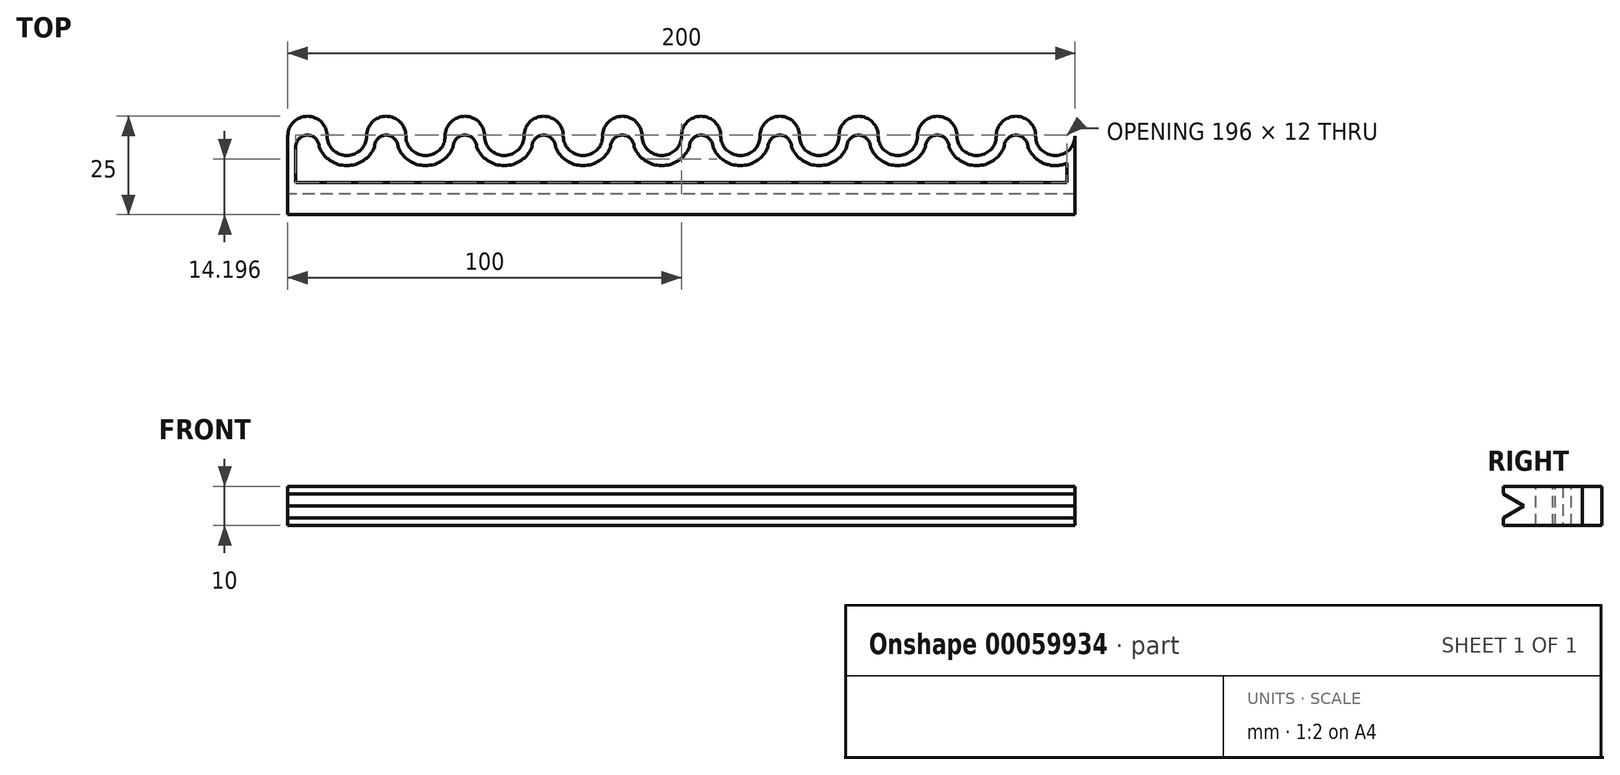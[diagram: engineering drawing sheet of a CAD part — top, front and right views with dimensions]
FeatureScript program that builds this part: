
annotation { "Feature Type Name" : "Feature", "Feature Type Description" : "" }
export const myFeature = defineFeature(function(context is Context, id is Id, definition is map)
    precondition{}
    {
        {
            var Q0;
            Q0=qCreatedBy(makeId("Top.planeOp"),FACE);
            var sketch = newSketch(context, id + "F0", { "sketchPlane" : qUnion([Q0])});
            skArc(sketch, "E0", {"start": v(10, 20) * mm, "mid": v(5, 25) * mm, "end": v(0, 20) * mm});
            skArc(sketch, "E1", {"start": v(10, 20) * mm, "mid": v(15, 15) * mm, "end": v(20, 20) * mm});
            skLineSegment(sketch, "E2", {"start": v(0, 20) * mm, "end": v(20, 20) * mm, "construction": true});
            skArc(sketch, "E3.1.0.0", {"start": v(30, 20) * mm, "mid": v(25, 25) * mm, "end": v(20, 20) * mm});
            skArc(sketch, "E3.1.0.1", {"start": v(30, 20) * mm, "mid": v(35, 15) * mm, "end": v(40, 20) * mm});
            skArc(sketch, "E3.2.0.0", {"start": v(50, 20) * mm, "mid": v(45, 25) * mm, "end": v(40, 20) * mm});
            skArc(sketch, "E3.2.0.1", {"start": v(50, 20) * mm, "mid": v(55, 15) * mm, "end": v(60, 20) * mm});
            skArc(sketch, "E3.3.0.0", {"start": v(70, 20) * mm, "mid": v(65, 25) * mm, "end": v(60, 20) * mm});
            skArc(sketch, "E3.3.0.1", {"start": v(70, 20) * mm, "mid": v(75, 15) * mm, "end": v(80, 20) * mm});
            skArc(sketch, "E3.4.0.0", {"start": v(90, 20) * mm, "mid": v(85, 25) * mm, "end": v(80, 20) * mm});
            skArc(sketch, "E3.4.0.1", {"start": v(90, 20) * mm, "mid": v(95, 15) * mm, "end": v(100, 20) * mm});
            skArc(sketch, "E3.5.0.0", {"start": v(110, 20) * mm, "mid": v(105, 25) * mm, "end": v(100, 20) * mm});
            skArc(sketch, "E3.5.0.1", {"start": v(110, 20) * mm, "mid": v(115, 15) * mm, "end": v(120, 20) * mm});
            skArc(sketch, "E3.6.0.0", {"start": v(130, 20) * mm, "mid": v(125, 25) * mm, "end": v(120, 20) * mm});
            skArc(sketch, "E3.6.0.1", {"start": v(130, 20) * mm, "mid": v(135, 15) * mm, "end": v(140, 20) * mm});
            skArc(sketch, "E3.7.0.0", {"start": v(150, 20) * mm, "mid": v(145, 25) * mm, "end": v(140, 20) * mm});
            skArc(sketch, "E3.7.0.1", {"start": v(150, 20) * mm, "mid": v(155, 15) * mm, "end": v(160, 20) * mm});
            skArc(sketch, "E3.8.0.0", {"start": v(170, 20) * mm, "mid": v(165, 25) * mm, "end": v(160, 20) * mm});
            skArc(sketch, "E3.8.0.1", {"start": v(170, 20) * mm, "mid": v(175, 15) * mm, "end": v(180, 20) * mm});
            skArc(sketch, "E3.9.0.0", {"start": v(190, 20) * mm, "mid": v(185, 25) * mm, "end": v(180, 20) * mm});
            skArc(sketch, "E3.9.0.1", {"start": v(190, 20) * mm, "mid": v(195, 15) * mm, "end": v(200, 20) * mm});
            skLineSegment(sketch, "E4", {"start": v(0, 20) * mm, "end": v(0, 0) * mm});
            skLineSegment(sketch, "E5", {"start": v(0, 0) * mm, "end": v(200, 0) * mm});
            skLineSegment(sketch, "E6", {"start": v(200, 0) * mm, "end": v(200, 20) * mm});
            skSolve(sketch);
        }
        {
            var Q0;
            Q0=makeQuery(id+"F0.imprint","IMPRINT",FACE,{"disambiguationData":[TD([[makeQuery(id+"F0.imprint","IMPRINT",EDGE,{"derivedFrom":sQuery(id+"F0.wireOp",EDGE,"E0")}),1.0]])]});
            extrude(context, id + "F1", {"entities" : qUnion([Q0]), "depth" : 10 * mm});
        }
        {
            var Q0;
            Q0=makeQuery(id+"F1.opExtrude","SWEPT_FACE",FACE,{"disambiguationData":[OSD([sQuery(id+"F0.wireOp",EDGE,"E4")])]});
            var sketch = newSketch(context, id + "F2", { "sketchPlane" : qUnion([Q0])});
            skLineSegment(sketch, "E7", {"start": v(0, 8) * mm, "end": v(-5.2, 5) * mm});
            skLineSegment(sketch, "E8", {"start": v(-5.2, 5) * mm, "end": v(0, 2) * mm});
            skLineSegment(sketch, "E9", {"start": v(0, 2) * mm, "end": v(0, 8) * mm});
            skLineSegment(sketch, "E10", {"start": v(0, 10) * mm, "end": v(0, 8) * mm});
            skLineSegment(sketch, "E11", {"start": v(0, 2) * mm, "end": v(0, 0) * mm});
            skSolve(sketch);
        }
        {
            var Q0;
            Q0=makeQuery(id+"F2.imprint","IMPRINT",FACE,{"disambiguationData":[TD([[makeQuery(id+"F2.imprint","IMPRINT",EDGE,{"derivedFrom":sQuery(id+"F2.wireOp",EDGE,"E7")}),1.0]])]});
            extrude(context, id + "F3", {"entities" : qUnion([Q0]), "operationType" : NewBodyOperationType.REMOVE, "endBound" : BoundingType.THROUGH_ALL, "oppositeDirection" : true, "depth" : 25 * mm});
        }
        {
            var Q0;
            Q0=makeQuery(id+"F1.opExtrude","CAP_FACE",FACE,{"disambiguationData":[OSD([sQuery(id+"F0.wireOp",EDGE,"E0"),sQuery(id+"F0.wireOp",EDGE,"E1"),sQuery(id+"F0.wireOp",EDGE,"E3.1.0.0"),sQuery(id+"F0.wireOp",EDGE,"E3.1.0.1"),sQuery(id+"F0.wireOp",EDGE,"E3.2.0.0"),sQuery(id+"F0.wireOp",EDGE,"E3.2.0.1"),sQuery(id+"F0.wireOp",EDGE,"E3.3.0.0"),sQuery(id+"F0.wireOp",EDGE,"E3.3.0.1"),sQuery(id+"F0.wireOp",EDGE,"E3.4.0.0"),sQuery(id+"F0.wireOp",EDGE,"E3.4.0.1"),sQuery(id+"F0.wireOp",EDGE,"E3.5.0.0"),sQuery(id+"F0.wireOp",EDGE,"E3.5.0.1"),sQuery(id+"F0.wireOp",EDGE,"E3.6.0.0"),sQuery(id+"F0.wireOp",EDGE,"E3.6.0.1"),sQuery(id+"F0.wireOp",EDGE,"E3.7.0.0"),sQuery(id+"F0.wireOp",EDGE,"E3.7.0.1"),sQuery(id+"F0.wireOp",EDGE,"E3.8.0.0"),sQuery(id+"F0.wireOp",EDGE,"E3.8.0.1"),sQuery(id+"F0.wireOp",EDGE,"E3.9.0.0"),sQuery(id+"F0.wireOp",EDGE,"E3.9.0.1"),sQuery(id+"F0.wireOp",EDGE,"E4"),sQuery(id+"F0.wireOp",EDGE,"E5"),sQuery(id+"F0.wireOp",EDGE,"E6")])],"isStart":false});
            var sketch = newSketch(context, id + "F4", { "sketchPlane" : qUnion([Q0])});
            skLineSegment(sketch, "E12", {"start": v(2, 17.2) * mm, "end": v(2, 8.2) * mm});
            skLineSegment(sketch, "E13", {"start": v(2, 8.2) * mm, "end": v(14.82, 8.2) * mm});
            skArc(sketch, "E14", {"start": v(8, 17.2) * mm, "mid": v(5, 20.2) * mm, "end": v(2, 17.2) * mm});
            skArc(sketch, "E15", {"start": v(28, 17.2) * mm, "mid": v(25, 20.2) * mm, "end": v(22, 17.2) * mm});
            skLineSegment(sketch, "E16", {"start": v(8, 17.2) * mm, "end": v(22, 17.2) * mm, "construction": true});
            skLineSegment(sketch, "E17", {"start": v(22, 17.2) * mm, "end": v(25, 17.2) * mm, "construction": true});
            skLineSegment(sketch, "E18", {"start": v(25, 17.2) * mm, "end": v(28, 17.2) * mm, "construction": true});
            skLineSegment(sketch, "E19", {"start": v(14.82, 8.2) * mm, "end": v(28, 8.2) * mm});
            skLineSegment(sketch, "E20", {"start": v(28, 8.2) * mm, "end": v(28, 17.2) * mm, "construction": true});
            skLineSegment(sketch, "E21", {"start": v(5, 25) * mm, "end": v(5, 17.2) * mm, "construction": true});
            skLineSegment(sketch, "E22", {"start": v(25, 25) * mm, "end": v(25, 17.2) * mm, "construction": true});
            skArc(sketch, "E23", {"start": v(8, 17.2) * mm, "mid": v(15, 12.46) * mm, "end": v(22, 17.2) * mm});
            skArc(sketch, "E24.1.0.0", {"start": v(48, 17.2) * mm, "mid": v(45, 20.2) * mm, "end": v(42, 17.2) * mm});
            skArc(sketch, "E24.1.0.1", {"start": v(28, 17.2) * mm, "mid": v(35, 12.46) * mm, "end": v(42, 17.2) * mm});
            skArc(sketch, "E24.2.0.0", {"start": v(68, 17.2) * mm, "mid": v(65, 20.2) * mm, "end": v(62, 17.2) * mm});
            skArc(sketch, "E24.2.0.1", {"start": v(48, 17.2) * mm, "mid": v(55, 12.46) * mm, "end": v(62, 17.2) * mm});
            skArc(sketch, "E24.3.0.0", {"start": v(88, 17.2) * mm, "mid": v(85, 20.2) * mm, "end": v(82, 17.2) * mm});
            skArc(sketch, "E24.3.0.1", {"start": v(68, 17.2) * mm, "mid": v(75, 12.46) * mm, "end": v(82, 17.2) * mm});
            skArc(sketch, "E24.4.0.0", {"start": v(108, 17.2) * mm, "mid": v(105, 20.2) * mm, "end": v(102, 17.2) * mm});
            skArc(sketch, "E24.4.0.1", {"start": v(88, 17.2) * mm, "mid": v(95, 12.46) * mm, "end": v(102, 17.2) * mm});
            skArc(sketch, "E24.5.0.0", {"start": v(128, 17.2) * mm, "mid": v(125, 20.2) * mm, "end": v(122, 17.2) * mm});
            skArc(sketch, "E24.5.0.1", {"start": v(108, 17.2) * mm, "mid": v(115, 12.46) * mm, "end": v(122, 17.2) * mm});
            skArc(sketch, "E24.6.0.0", {"start": v(148, 17.2) * mm, "mid": v(145, 20.2) * mm, "end": v(142, 17.2) * mm});
            skArc(sketch, "E24.6.0.1", {"start": v(128, 17.2) * mm, "mid": v(135, 12.46) * mm, "end": v(142, 17.2) * mm});
            skArc(sketch, "E24.7.0.0", {"start": v(168, 17.2) * mm, "mid": v(165, 20.2) * mm, "end": v(162, 17.2) * mm});
            skArc(sketch, "E24.7.0.1", {"start": v(148, 17.2) * mm, "mid": v(155, 12.46) * mm, "end": v(162, 17.2) * mm});
            skArc(sketch, "E24.8.0.0", {"start": v(188, 17.2) * mm, "mid": v(185, 20.2) * mm, "end": v(182, 17.2) * mm});
            skArc(sketch, "E24.8.0.1", {"start": v(168, 17.2) * mm, "mid": v(175, 12.46) * mm, "end": v(182, 17.2) * mm});
            skLineSegment(sketch, "E24.direction1", {"start": v(22, 17.2) * mm, "end": v(42, 17.2) * mm, "construction": true});
            skArc(sketch, "E25", {"start": v(188, 17.2) * mm, "mid": v(192.13, 13.03) * mm, "end": v(198, 13.08) * mm});
            skLineSegment(sketch, "E26", {"start": v(198, 13.08) * mm, "end": v(198, 8.2) * mm});
            skLineSegment(sketch, "E27", {"start": v(28, 8.2) * mm, "end": v(198, 8.2) * mm});
            skSolve(sketch);
        }
        {
            var Q0;
            Q0=makeQuery(id+"F4.imprint","IMPRINT",FACE,{"disambiguationData":[TD([[makeQuery(id+"F4.imprint","IMPRINT",EDGE,{"derivedFrom":sQuery(id+"F4.wireOp",EDGE,"E12")}),1.0]])]});
            extrude(context, id + "F5", {"entities" : qUnion([Q0]), "operationType" : NewBodyOperationType.REMOVE, "endBound" : BoundingType.UP_TO_NEXT, "oppositeDirection" : true, "depth" : 25 * mm});
        }
    });
